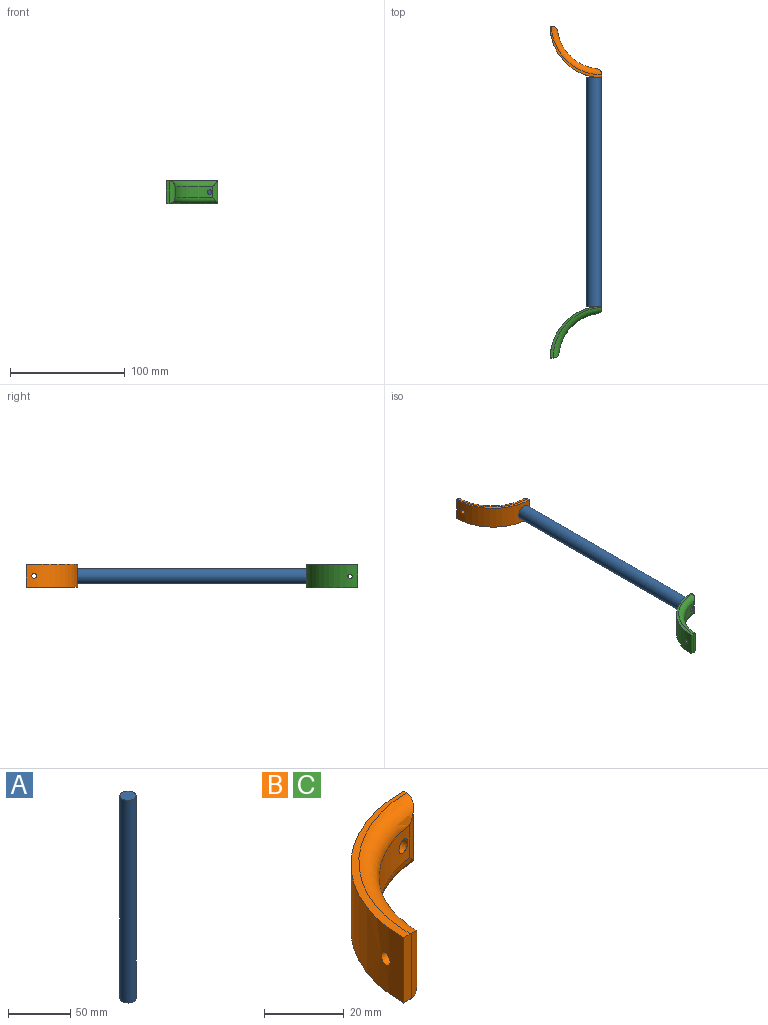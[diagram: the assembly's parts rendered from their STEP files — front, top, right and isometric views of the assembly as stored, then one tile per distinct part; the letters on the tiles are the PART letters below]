
ASSEMBLY  parts=3 mates=2
PART A: 3 faces, bbox 13x13x200 mm
  f0: cylinder r=6.5mm len=200mm, axis (0,0,-1), area 8168.1mm2, adj f1,f2
  f1: plane 13x13mm, normal (0,0,1), area 132.7mm2, adj f0
  f2: plane 13x13mm, normal (0,0,-1), area 132.7mm2, adj f0
PART B: 12 faces, bbox 50.2x51.4x20 mm
  f0: cylinder r=39mm len=34.15mm, axis (0,0,-1), area 487mm2, adj f6,f7,f8,f9,f10,f11
  f1: plane 20x1.47mm, normal (1,0,0), area 29.4mm2, adj f2,f4,f5,f7,f8,f9
  f2: cylinder r=45mm len=45mm, axis (0,0,-1), area 1389.7mm2, adj f1,f3,f4,f5,f10,f11
  f3: plane 20x2.69mm, normal (0,-1,0), area 53.8mm2, adj f2,f4,f5,f6,f7,f8
  f4: plane 45x45mm, normal (0,0,1), area 131.8mm2, adj f1,f2,f3,f7
  f5: plane 45x45mm, normal (0,0,-1), area 131.8mm2, adj f1,f2,f3,f8
  f6: cylinder r=5mm len=19.98mm, axis (0,0,-1), area 118.6mm2, adj f0,f3,f7,f8
  f7: torus R=44mm, axis (0,0,1), area 468.8mm2, adj f0,f1,f3,f4,f6,f9
  f8: torus R=44mm, axis (0,0,1), area 468.8mm2, adj f0,f1,f3,f5,f6,f9
  f9: cylinder r=5mm len=19.96mm, axis (0,0,-1), area 115.4mm2, adj f0,f1,f7,f8
  f10: cylinder r=1.88mm len=8.12mm, axis (1,0,0), area 88.5mm2, adj f0,f2
  f11: cylinder r=2mm len=7.14mm, axis (0,-1,0), area 80.1mm2, adj f0,f2
PART C: same geometry as B
PLACE A rot(axis=(-1,0,0),90deg) t=(-32.33,-44.43,-4.96)mm
PLACE B rot(axis=(0,0,1),90deg) t=(-25.45,100.34,-14.84)mm
PLACE C t=(-25.33,-189.19,-14.96)mm
MATE fastened B.f10 <-> A.f0  axis (0,1,0) through (-32.33,55.57,-4.96)mm
MATE fastened C.f11 <-> A.f0  axis (0,-1,0) through (-32.33,-144.43,-4.96)mm
